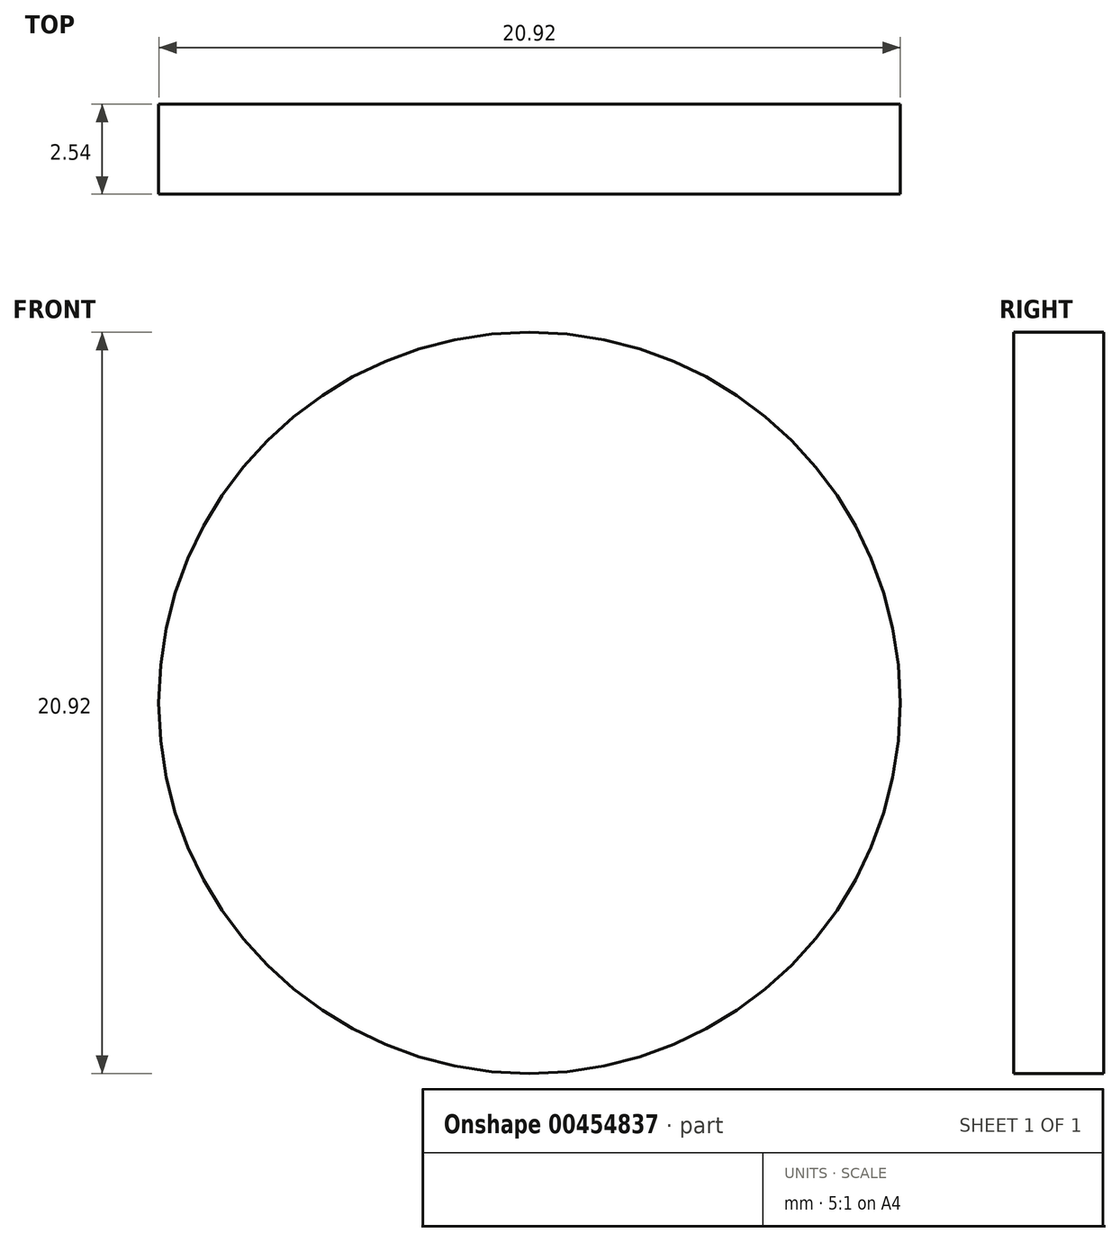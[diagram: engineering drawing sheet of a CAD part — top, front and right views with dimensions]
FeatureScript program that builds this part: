
annotation { "Feature Type Name" : "Feature", "Feature Type Description" : "" }
export const myFeature = defineFeature(function(context is Context, id is Id, definition is map)
    precondition{}
    {
        {
            var Q0;
            Q0=qCreatedBy(makeId("Front.planeOp"),FACE);
            var sketch = newSketch(context, id + "F0", { "sketchPlane" : qUnion([Q0])});
            skCircle(sketch, "E0", {"center": v(0, 0) * mm, "radius": 10.46 * mm});
            skSolve(sketch);
        }
        {
            var Q0;
            Q0 = qSketchRegion(id + "F0", true);
            extrude(context, id + "F1", {"entities" : qUnion([Q0]), "depth" : 2.54 * mm, "offsetDistance" : 25.4 * mm});
        }
    });
